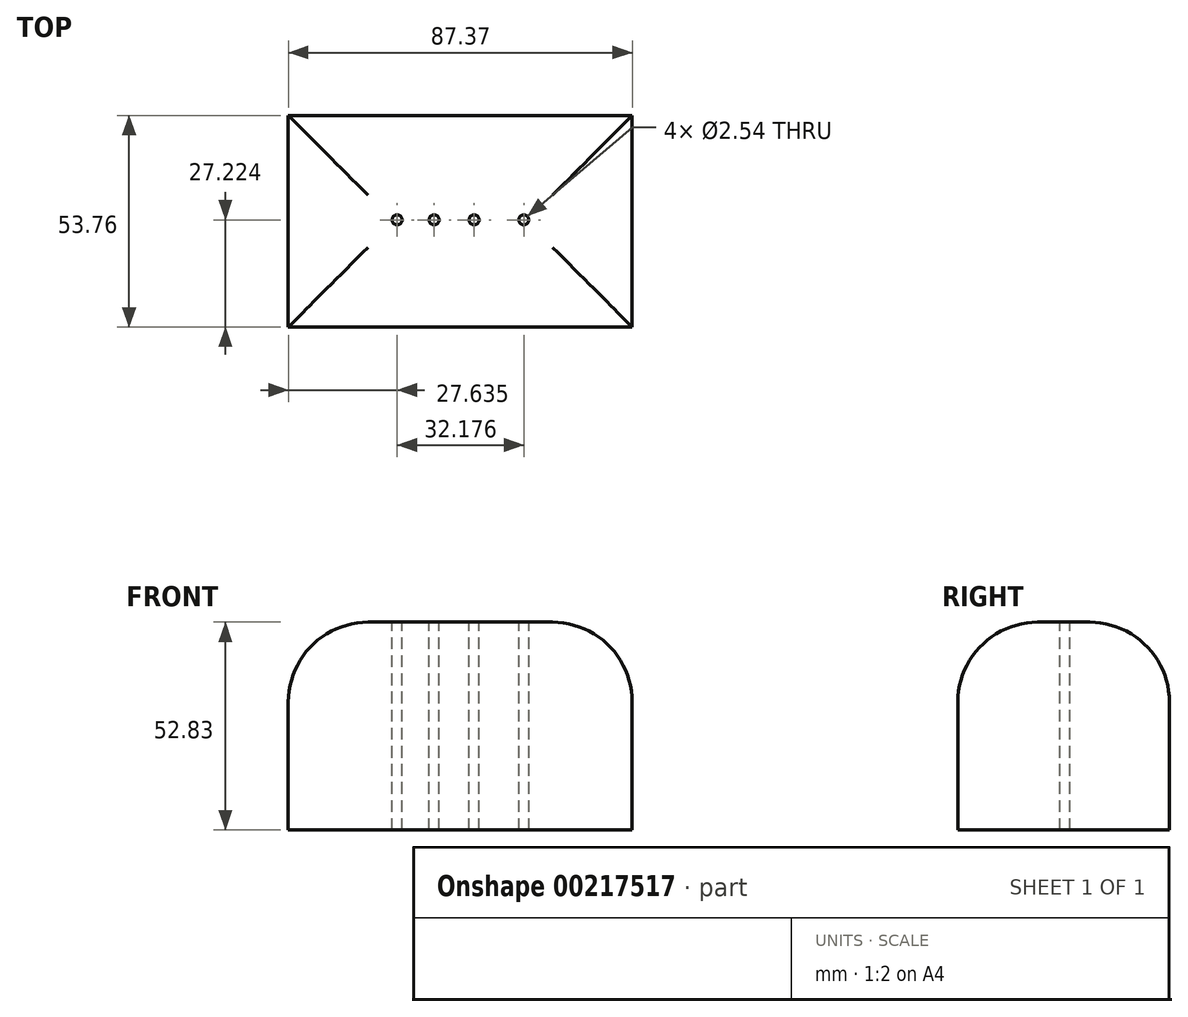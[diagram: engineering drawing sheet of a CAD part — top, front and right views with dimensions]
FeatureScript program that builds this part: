
annotation { "Feature Type Name" : "Feature", "Feature Type Description" : "" }
export const myFeature = defineFeature(function(context is Context, id is Id, definition is map)
    precondition{}
    {
        {
            var Q0;
            Q0=qCreatedBy(makeId("Top.planeOp"),FACE);
            var sketch = newSketch(context, id + "F0", { "sketchPlane" : qUnion([Q0])});
            skLineSegment(sketch, "E0.bottom", {"start": v(-43.06, 24.96) * mm, "end": v(44.3, 24.96) * mm});
            skLineSegment(sketch, "E0.top", {"start": v(-43.06, -28.8) * mm, "end": v(44.3, -28.8) * mm});
            skLineSegment(sketch, "E0.left", {"start": v(-43.06, 24.96) * mm, "end": v(-43.06, -28.8) * mm});
            skLineSegment(sketch, "E0.right", {"start": v(44.3, 24.96) * mm, "end": v(44.3, -28.8) * mm});
            skSolve(sketch);
        }
        {
            var Q0;
            Q0 = qSketchRegion(id + "F0", true);
            extrude(context, id + "F1", {"entities" : qUnion([Q0]), "depth" : 52.83 * mm});
        }
        {
            var Q0;
            Q0=makeQuery(id+"F1.opExtrude","CAP_EDGE",EDGE,{"disambiguationData":[OSD([sQuery(id+"F0.wireOp",EDGE,"E0.top")])],"isStart":false});
            var Q1;
            Q1=makeQuery(id+"F1.opExtrude","CAP_EDGE",EDGE,{"disambiguationData":[OSD([sQuery(id+"F0.wireOp",EDGE,"E0.bottom")])],"isStart":false});
            var Q2;
            Q2=makeQuery(id+"F1.opExtrude","CAP_EDGE",EDGE,{"disambiguationData":[OSD([sQuery(id+"F0.wireOp",EDGE,"E0.right")])],"isStart":false});
            var Q3;
            Q3=makeQuery(id+"F1.opExtrude","CAP_EDGE",EDGE,{"disambiguationData":[OSD([sQuery(id+"F0.wireOp",EDGE,"E0.left")])],"isStart":false});
            fillet(context, id + "F2", {"entities" : qUnion([Q0, Q1, Q2, Q3]), "radius" : 20.24 * mm, "tangentPropagation" : true, "allowEdgeOverflow" : false});
        }
        {
            var Q0;
            Q0=makeQuery(id+"F1.opExtrude","CAP_FACE",FACE,{"disambiguationData":[OSD([sQuery(id+"F0.wireOp",EDGE,"E0.bottom"),sQuery(id+"F0.wireOp",EDGE,"E0.top"),sQuery(id+"F0.wireOp",EDGE,"E0.left"),sQuery(id+"F0.wireOp",EDGE,"E0.right")])],"isStart":false});
            var sketch = newSketch(context, id + "F3", { "sketchPlane" : qUnion([Q0])});
            skPoint(sketch, "E1", {"position": v(-15.42, -1.58) * mm});
            skPoint(sketch, "E2", {"position": v(-6.02, -1.58) * mm});
            skPoint(sketch, "E3", {"position": v(4.14, -1.58) * mm});
            skPoint(sketch, "E4", {"position": v(16.75, -1.58) * mm});
            skSolve(sketch);
        }
        {
            var Q0;
            Q0=sQuery(id+"F3.wireOp",VERTEX,"E1");
            var Q1;
            Q1=sQuery(id+"F3.wireOp",VERTEX,"E2");
            var Q2;
            Q2=sQuery(id+"F3.wireOp",VERTEX,"E3");
            var Q3;
            Q3=sQuery(id+"F3.wireOp",VERTEX,"E4");
            var Q4;
            Q4=makeQuery(id+"F1.opExtrude","SWEPT_BODY",BODY,{"disambiguationData":[OSD([sQuery(id+"F0.wireOp",EDGE,"E0.bottom"),sQuery(id+"F0.wireOp",EDGE,"E0.top"),sQuery(id+"F0.wireOp",EDGE,"E0.left"),sQuery(id+"F0.wireOp",EDGE,"E0.right")])]});
            hole(context, id + "F4", {"style" : HoleStyle.SIMPLE, "endStyle" : HoleEndStyle.THROUGH, "holeDiameter" : 2.54 * mm, "locations" : qUnion([Q0, Q1, Q2, Q3]), "scope" : qUnion([Q4]), "isTappedThrough" : true});
        }
    });
